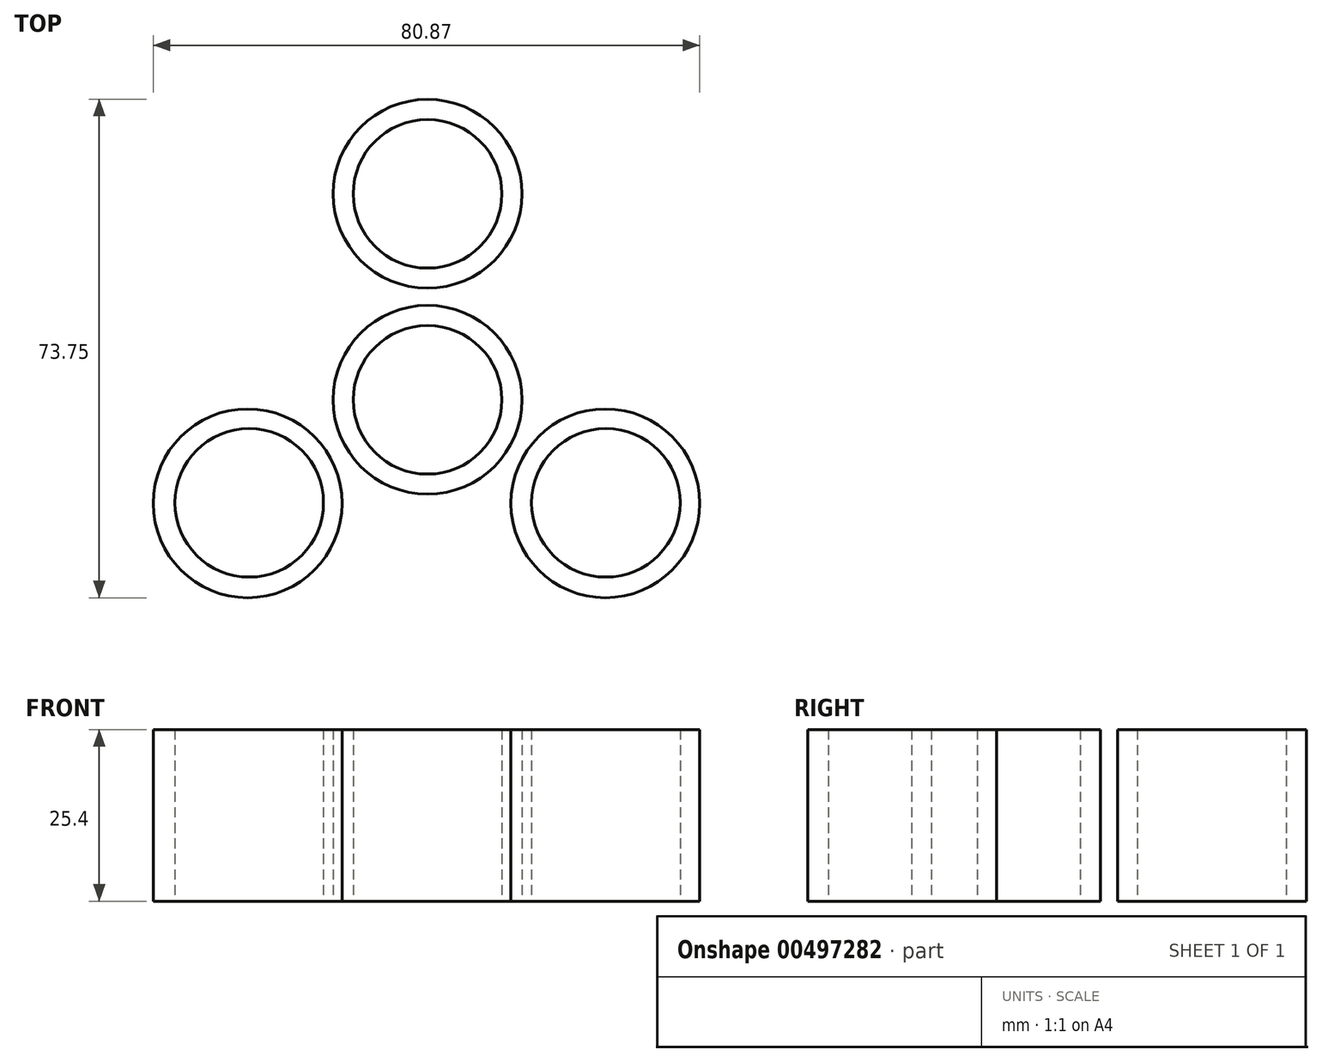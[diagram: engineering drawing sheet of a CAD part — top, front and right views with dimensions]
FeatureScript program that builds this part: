
annotation { "Feature Type Name" : "Feature", "Feature Type Description" : "" }
export const myFeature = defineFeature(function(context is Context, id is Id, definition is map)
    precondition{}
    {
        {
            var Q0;
            Q0=qCreatedBy(makeId("Top.planeOp"),FACE);
            var sketch = newSketch(context, id + "F0", { "sketchPlane" : qUnion([Q0])});
            skCircle(sketch, "E0", {"center": v(0, 0) * mm, "radius": 44.45 * mm});
            skCircle(sketch, "E1", {"center": v(0, 0) * mm, "radius": 11 * mm});
            skLineSegment(sketch, "E2", {"start": v(0, 0) * mm, "end": v(0, 30.48) * mm});
            skCircle(sketch, "E3", {"center": v(0, 30.48) * mm, "radius": 11 * mm});
            skCircle(sketch, "E4.1.0", {"center": v(-26.4, -15.24) * mm, "radius": 11 * mm});
            skCircle(sketch, "E4.2.0", {"center": v(26.4, -15.24) * mm, "radius": 11 * mm});
            skSolve(sketch);
        }
        {
            var Q0;
            Q0=qCreatedBy(makeId("Top.planeOp"),FACE);
            var sketch = newSketch(context, id + "F1", { "sketchPlane" : qUnion([Q0])});
            skCircle(sketch, "E5", {"center": v(0, 0) * mm, "radius": 13.97 * mm});
            skCircle(sketch, "E6", {"center": v(-26.62, -15.32) * mm, "radius": 13.97 * mm});
            skCircle(sketch, "E7", {"center": v(0, 30.49) * mm, "radius": 13.97 * mm});
            skCircle(sketch, "E8", {"center": v(26.3, -15.32) * mm, "radius": 13.97 * mm});
            skSolve(sketch);
        }
        {
            var Q0;
            Q0=qCreatedBy(makeId("Top.planeOp"),FACE);
            var sketch = newSketch(context, id + "F2", { "sketchPlane" : qUnion([Q0])});
            skSolve(sketch);
        }
        {
            var Q0;
            Q0 = qSketchRegion(id + "F2", true);
            var Q1;
            Q1=makeQuery(id+"F0.imprint","IMPRINT",FACE,{"disambiguationData":[TD([[makeQuery(id+"F0.imprint","IMPRINT",EDGE,{"derivedFrom":sQuery(id+"F0.wireOp",EDGE,"E4.1.0")}),1.0]])]});
            var Q2;
            Q2=makeQuery(id+"F0.imprint","IMPRINT",FACE,{"disambiguationData":[TD([[makeQuery(id+"F0.imprint","IMPRINT",EDGE,{"derivedFrom":sQuery(id+"F0.wireOp",EDGE,"E1")}),1.0]])]});
            var Q3;
            Q3=makeQuery(id+"F1.imprint","IMPRINT",FACE,{"disambiguationData":[TD([[makeQuery(id+"F1.imprint","IMPRINT",EDGE,{"derivedFrom":sQuery(id+"F1.wireOp",EDGE,"E5")}),1.0]])]});
            var Q4;
            Q4=makeQuery(id+"F1.imprint","IMPRINT",FACE,{"disambiguationData":[TD([[makeQuery(id+"F1.imprint","IMPRINT",EDGE,{"derivedFrom":sQuery(id+"F1.wireOp",EDGE,"E7")}),1.0]])]});
            var Q5;
            Q5=makeQuery(id+"F0.imprint","IMPRINT",FACE,{"disambiguationData":[TD([[makeQuery(id+"F0.imprint","IMPRINT",EDGE,{"derivedFrom":sQuery(id+"F0.wireOp",EDGE,"E3")}),1.0]])]});
            var Q6;
            Q6=makeQuery(id+"F1.imprint","IMPRINT",FACE,{"disambiguationData":[TD([[makeQuery(id+"F1.imprint","IMPRINT",EDGE,{"derivedFrom":sQuery(id+"F1.wireOp",EDGE,"E6")}),1.0]])]});
            var Q7;
            Q7=makeQuery(id+"F0.imprint","IMPRINT",FACE,{"disambiguationData":[TD([[makeQuery(id+"F0.imprint","IMPRINT",EDGE,{"derivedFrom":sQuery(id+"F0.wireOp",EDGE,"E4.2.0")}),1.0]])]});
            extrude(context, id + "F3", {"entities" : qUnion([Q0, Q1, Q2, Q3, Q4, Q5, Q6, Q7]), "depth" : 25.4 * mm});
        }
        {
            var Q0;
            Q0 = qSketchRegion(id + "F1", true);
            extrude(context, id + "F4", {"entities" : qUnion([Q0]), "depth" : 25.4 * mm});
        }
    });
